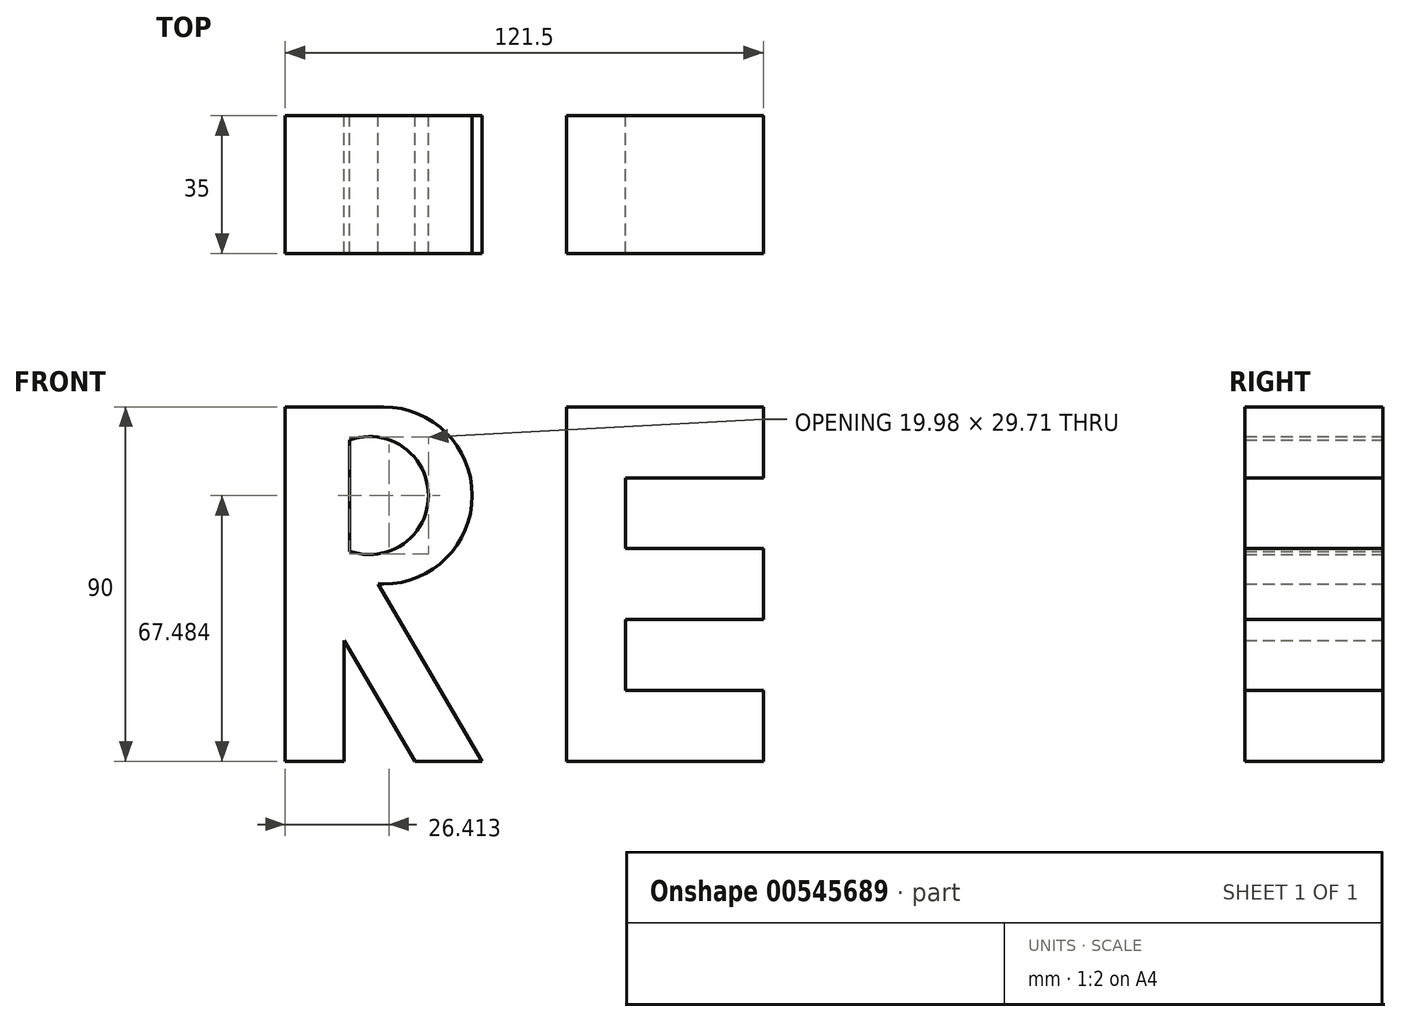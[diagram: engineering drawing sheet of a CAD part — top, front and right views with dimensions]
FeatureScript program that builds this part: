
annotation { "Feature Type Name" : "Feature", "Feature Type Description" : "" }
export const myFeature = defineFeature(function(context is Context, id is Id, definition is map)
    precondition{}
    {
        {
            var Q0;
            Q0=qCreatedBy(makeId("Front.planeOp"),FACE);
            var sketch = newSketch(context, id + "F0", { "sketchPlane" : qUnion([Q0])});
            skLineSegment(sketch, "E0", {"start": v(-63.5, 45) * mm, "end": v(-63.5, -45) * mm});
            skLineSegment(sketch, "E1", {"start": v(-63.5, 45) * mm, "end": v(-38.5, 45) * mm});
            skArc(sketch, "E2", {"start": v(-38.5, 0) * mm, "mid": v(-16, 22.5) * mm, "end": v(-38.5, 45) * mm});
            skLineSegment(sketch, "E3", {"start": v(-63.5, -45) * mm, "end": v(-48.5, -45) * mm});
            skLineSegment(sketch, "E4", {"start": v(-48.5, -45) * mm, "end": v(-48.5, -14.32) * mm});
            skLineSegment(sketch, "E5", {"start": v(-48.5, -14.32) * mm, "end": v(-30.5, -45) * mm});
            skLineSegment(sketch, "E6", {"start": v(-30.5, -45) * mm, "end": v(-13.5, -45) * mm});
            skLineSegment(sketch, "E7", {"start": v(-13.5, -45) * mm, "end": v(-39.9, 0) * mm});
            skLineSegment(sketch, "E8", {"start": v(-39.9, 0) * mm, "end": v(-38.5, 0) * mm});
            skLineSegment(sketch, "E9", {"start": v(-47.08, 36.63) * mm, "end": v(-47.08, 8.33) * mm});
            skArc(sketch, "E10", {"start": v(-47.08, 8.33) * mm, "mid": v(-27.1, 22.48) * mm, "end": v(-47.08, 36.63) * mm});
            skLineSegment(sketch, "E11", {"start": v(7.99, -45) * mm, "end": v(57.99, -45) * mm});
            skLineSegment(sketch, "E12", {"start": v(57.99, -45) * mm, "end": v(57.99, -27) * mm});
            skLineSegment(sketch, "E13", {"start": v(7.99, -45) * mm, "end": v(7.99, 45) * mm});
            skLineSegment(sketch, "E14", {"start": v(7.99, 45) * mm, "end": v(57.99, 45) * mm});
            skLineSegment(sketch, "E15", {"start": v(57.99, 45) * mm, "end": v(57.99, 27) * mm});
            skLineSegment(sketch, "E16", {"start": v(57.99, 27) * mm, "end": v(22.91, 27) * mm});
            skLineSegment(sketch, "E17", {"start": v(22.91, 27) * mm, "end": v(22.91, 9) * mm});
            skLineSegment(sketch, "E18", {"start": v(22.91, 9) * mm, "end": v(57.99, 9) * mm});
            skLineSegment(sketch, "E19", {"start": v(57.99, 9) * mm, "end": v(57.99, -9) * mm});
            skLineSegment(sketch, "E20", {"start": v(57.99, -9) * mm, "end": v(22.91, -9) * mm});
            skLineSegment(sketch, "E21", {"start": v(22.91, -9) * mm, "end": v(22.91, -27) * mm});
            skLineSegment(sketch, "E22", {"start": v(22.91, -27) * mm, "end": v(57.99, -27) * mm});
            skSolve(sketch);
        }
        {
            var Q0;
            Q0 = qSketchRegion(id + "F0", true);
            extrude(context, id + "F1", {"entities" : qUnion([Q0]), "depth" : 35 * mm, "offsetDistance" : 25 * mm});
        }
    });
